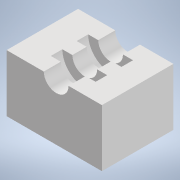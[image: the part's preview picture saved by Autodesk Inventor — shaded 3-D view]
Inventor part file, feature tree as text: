
AUTODESK INVENTOR PART (.ipt)
format: ipt  version: 2021 (Build 250183000, 183)  size: 167,424 bytes
history: native  units: in
note: dims shown in document units (in); Inventor stores cm internally (conversion verified against a paired STEP export)
features: extrude x8, sketch x8
ambient origin geometry x8: Origin, YZ Plane, XZ Plane, XY Plane, X Axis, Y Axis, Z Axis, Center Point
bodies: Solid2 (feature_tree)
feature tree (16):
  extrude  "Extrusion1"  Depth=2.9528in
  extrude  "Extrusion2"  Depth=2.3622in
  sketch  "Sketch3"  dims[d5=0.1969in d6=0.1969in]
  extrude  "Extrusion14"  Depth=0.1969in
  extrude  "Extrusion15"  Depth=2.3228in TaperAngle=0.0deg
  extrude  "Extrusion16"  Depth=2.3622in
  extrude  "Extrusion17"  Depth=2.3228in TaperAngle=0.0deg
  extrude  "Extrusion18"  Depth=0.4764in TaperAngle=0.0deg
  extrude  "Extrusion19"  Depth=2.9528in TaperAngle=0.0deg
  sketch  "Sketch1"  dims[d0=3.937in d1=2.9528in]
  sketch  "Sketch2"  dims[d2=2.3622in d3=0.0in d4=0.1969in]
  sketch  "Sketch13"  dims[d7=0.1969in d8=2.3228in d9=0.0in]
  sketch  "Sketch14"  dims[d10=1.0236in d11=2.3622in]
  sketch  "Sketch15"  dims[d44=0.9843in d45=2.3228in d46=0.0in]
  sketch  "Sketch16"  dims[d47=1.8508in d48=0.4764in d49=0.0in]
  sketch  "Sketch17"  dims[d50=0.9843in d51=2.3228in d52=0.0in d53=1.8508in d54=0.4764in d55=0.0in d56=2.3228in d57=0.0in d58=2.9528in d59=0.0in]
